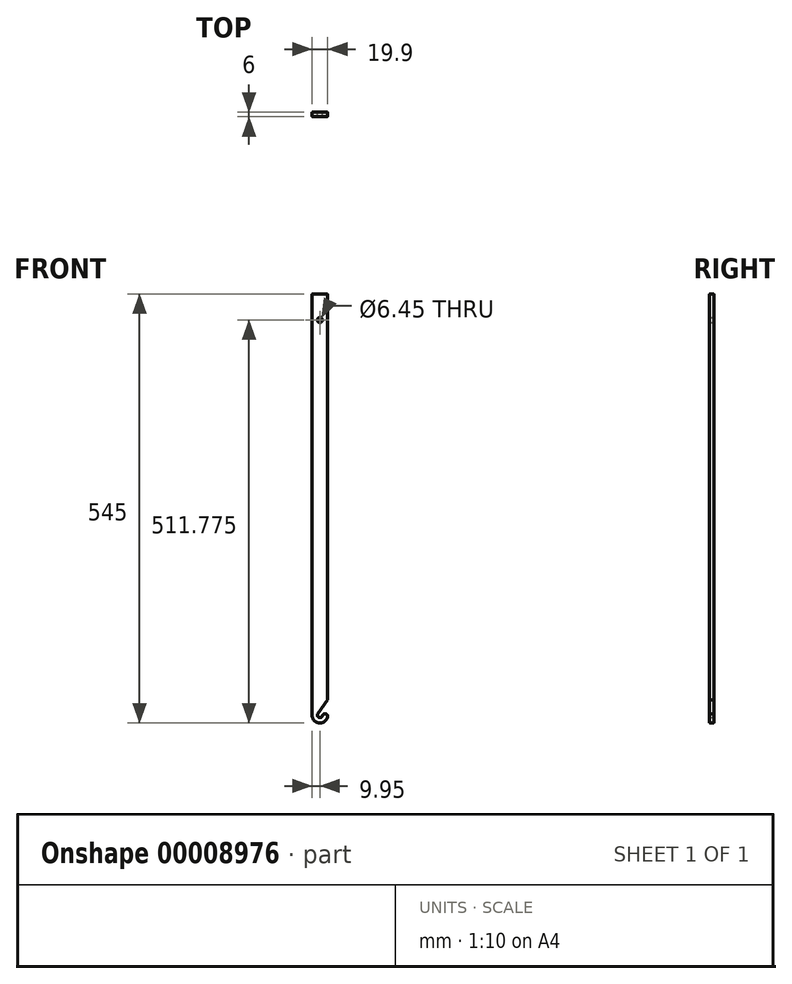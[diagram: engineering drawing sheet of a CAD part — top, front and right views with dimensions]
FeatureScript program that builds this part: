
annotation { "Feature Type Name" : "Feature", "Feature Type Description" : "" }
export const myFeature = defineFeature(function(context is Context, id is Id, definition is map)
    precondition{}
    {
        {
            var Q0;
            Q0=qCreatedBy(makeId("Front.planeOp"),FACE);
            var sketch = newSketch(context, id + "F0", { "sketchPlane" : qUnion([Q0])});
            skLineSegment(sketch, "E0.rect.bottom", {"start": v(9.95, 272.5) * mm, "end": v(-9.95, 272.5) * mm});
            skLineSegment(sketch, "E0.rect.left", {"start": v(9.95, 272.5) * mm, "end": v(9.95, -243.3) * mm});
            skLineSegment(sketch, "E0.rect.right", {"start": v(-9.95, 272.5) * mm, "end": v(-9.95, -262.55) * mm});
            skPoint(sketch, "E0.rect.middle", {"position": v(0, 0) * mm});
            skCircle(sketch, "E1", {"center": v(0, 239.28) * mm, "radius": 3.23 * mm});
            skArc(sketch, "E2", {"start": v(-2.61, -260.66) * mm, "mid": v(-1.36, -265.48) * mm, "end": v(3.13, -263.32) * mm});
            skArc(sketch, "E3", {"start": v(-9.95, -262.55) * mm, "mid": v(-1.2, -272.43) * mm, "end": v(9.66, -264.94) * mm});
            skLineSegment(sketch, "E4", {"start": v(-2.61, -260.66) * mm, "end": v(9.95, -243.3) * mm});
            skArc(sketch, "E5", {"start": v(9.66, -264.94) * mm, "mid": v(7.2, -260.87) * mm, "end": v(3.13, -263.32) * mm});
            skPoint(sketch, "E6.orphan", {"position": v(-9.95, -272.5) * mm});
            skPoint(sketch, "E0.rect.top.start.orphan", {"position": v(9.95, -272.5) * mm});
            skSolve(sketch);
        }
        {
            var Q0;
            Q0=makeQuery(id+"F0.imprint","IMPRINT",FACE,{"disambiguationData":[TD([[makeQuery(id+"F0.imprint","IMPRINT",EDGE,{"derivedFrom":sQuery(id+"F0.wireOp",EDGE,"E0.rect.bottom")}),1.0]])]});
            extrude(context, id + "F1", {"entities" : qUnion([Q0]), "depth" : 6 * mm, "symmetric" : true});
        }
        {
            var Q0;
            Q0=makeQuery(id+"F1.opExtrude","CAP_EDGE",EDGE,{"disambiguationData":[OSD([sQuery(id+"F0.wireOp",EDGE,"E0.rect.left")])],"isStart":false});
            var Q1;
            Q1=makeQuery(id+"F1.opExtrude","CAP_EDGE",EDGE,{"disambiguationData":[OSD([sQuery(id+"F0.wireOp",EDGE,"E0.rect.right")])],"isStart":false});
            var Q2;
            Q2=makeQuery(id+"F1.opExtrude","CAP_EDGE",EDGE,{"disambiguationData":[OSD([sQuery(id+"F0.wireOp",EDGE,"E0.rect.right")])],"isStart":true});
            var Q3;
            Q3=makeQuery(id+"F1.opExtrude","CAP_EDGE",EDGE,{"disambiguationData":[OSD([sQuery(id+"F0.wireOp",EDGE,"E0.rect.left")])],"isStart":true});
            var Q4;
            Q4=makeQuery(id+"F1.opExtrude","CAP_EDGE",EDGE,{"disambiguationData":[OSD([sQuery(id+"F0.wireOp",EDGE,"E1")])],"isStart":true});
            var Q5;
            Q5=makeQuery(id+"F1.opExtrude","CAP_EDGE",EDGE,{"disambiguationData":[OSD([sQuery(id+"F0.wireOp",EDGE,"E1")])],"isStart":false});
            var Q6;
            Q6=makeQuery(id+"F1.opExtrude","CAP_EDGE",EDGE,{"disambiguationData":[OSD([sQuery(id+"F0.wireOp",EDGE,"E0.rect.bottom")])],"isStart":true});
            var Q7;
            Q7=makeQuery(id+"F1.opExtrude","SWEPT_EDGE",EDGE,{"disambiguationData":[OSD([sQuery(id+"F0.wireOp",EDGE,"E0.rect.bottom"),sQuery(id+"F0.wireOp",EDGE,"E0.rect.right")])]});
            var Q8;
            Q8=makeQuery(id+"F1.opExtrude","CAP_EDGE",EDGE,{"disambiguationData":[OSD([sQuery(id+"F0.wireOp",EDGE,"E0.rect.bottom")])],"isStart":false});
            var Q9;
            Q9=makeQuery(id+"F1.opExtrude","SWEPT_EDGE",EDGE,{"disambiguationData":[OSD([sQuery(id+"F0.wireOp",EDGE,"E0.rect.bottom"),sQuery(id+"F0.wireOp",EDGE,"E0.rect.left")])]});
            fillet(context, id + "F2", {"entities" : qUnion([Q0, Q1, Q2, Q3, Q4, Q5, Q6, Q7, Q8, Q9]), "radius" : 1 * mm, "tangentPropagation" : true, "allowEdgeOverflow" : false});
        }
    });
